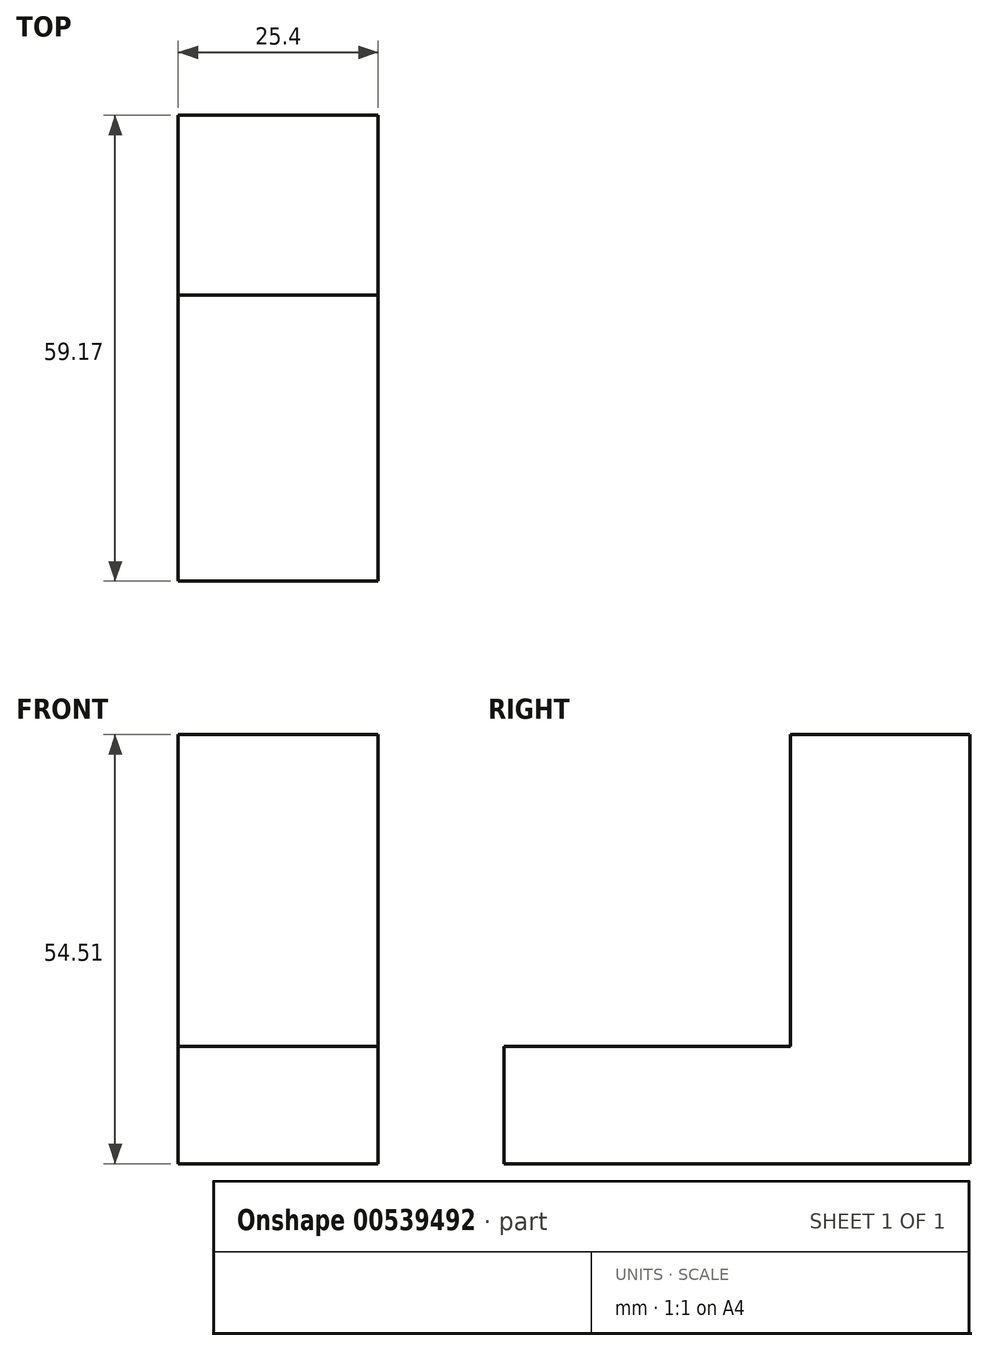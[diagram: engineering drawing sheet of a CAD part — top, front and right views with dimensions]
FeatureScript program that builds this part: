
annotation { "Feature Type Name" : "Feature", "Feature Type Description" : "" }
export const myFeature = defineFeature(function(context is Context, id is Id, definition is map)
    precondition{}
    {
        {
            var Q0;
            Q0=qCreatedBy(makeId("Right.planeOp"),FACE);
            var sketch = newSketch(context, id + "F0", { "sketchPlane" : qUnion([Q0])});
            skLineSegment(sketch, "E0", {"start": v(0, 0) * mm, "end": v(0, 54.51) * mm});
            skLineSegment(sketch, "E1", {"start": v(-22.83, 54.51) * mm, "end": v(0, 54.51) * mm});
            skLineSegment(sketch, "E2", {"start": v(-22.83, 14.9) * mm, "end": v(-22.83, 54.51) * mm});
            skLineSegment(sketch, "E3", {"start": v(-22.83, 14.9) * mm, "end": v(-59.17, 14.9) * mm});
            skLineSegment(sketch, "E4", {"start": v(-59.17, 0) * mm, "end": v(-59.17, 14.9) * mm});
            skLineSegment(sketch, "E5", {"start": v(-59.17, 0) * mm, "end": v(0, 0) * mm});
            skSolve(sketch);
        }
        {
            var Q0;
            Q0=makeQuery(id+"F0.imprint","IMPRINT",FACE,{"disambiguationData":[TD([[makeQuery(id+"F0.imprint","IMPRINT",EDGE,{"derivedFrom":sQuery(id+"F0.wireOp",EDGE,"E0")}),1.0]])]});
            var sketch = newSketch(context, id + "F1", { "sketchPlane" : qUnion([Q0])});
            skSolve(sketch);
        }
        {
            var Q0;
            Q0 = qSketchRegion(id + "F1", true);
            var Q1;
            Q1=makeQuery(id+"F0.imprint","IMPRINT",FACE,{"disambiguationData":[TD([[makeQuery(id+"F0.imprint","IMPRINT",EDGE,{"derivedFrom":sQuery(id+"F0.wireOp",EDGE,"E0")}),1.0]])]});
            extrude(context, id + "F2", {"entities" : qUnion([Q0, Q1]), "depth" : 25.4 * mm, "offsetDistance" : 25.4 * mm});
        }
    });
